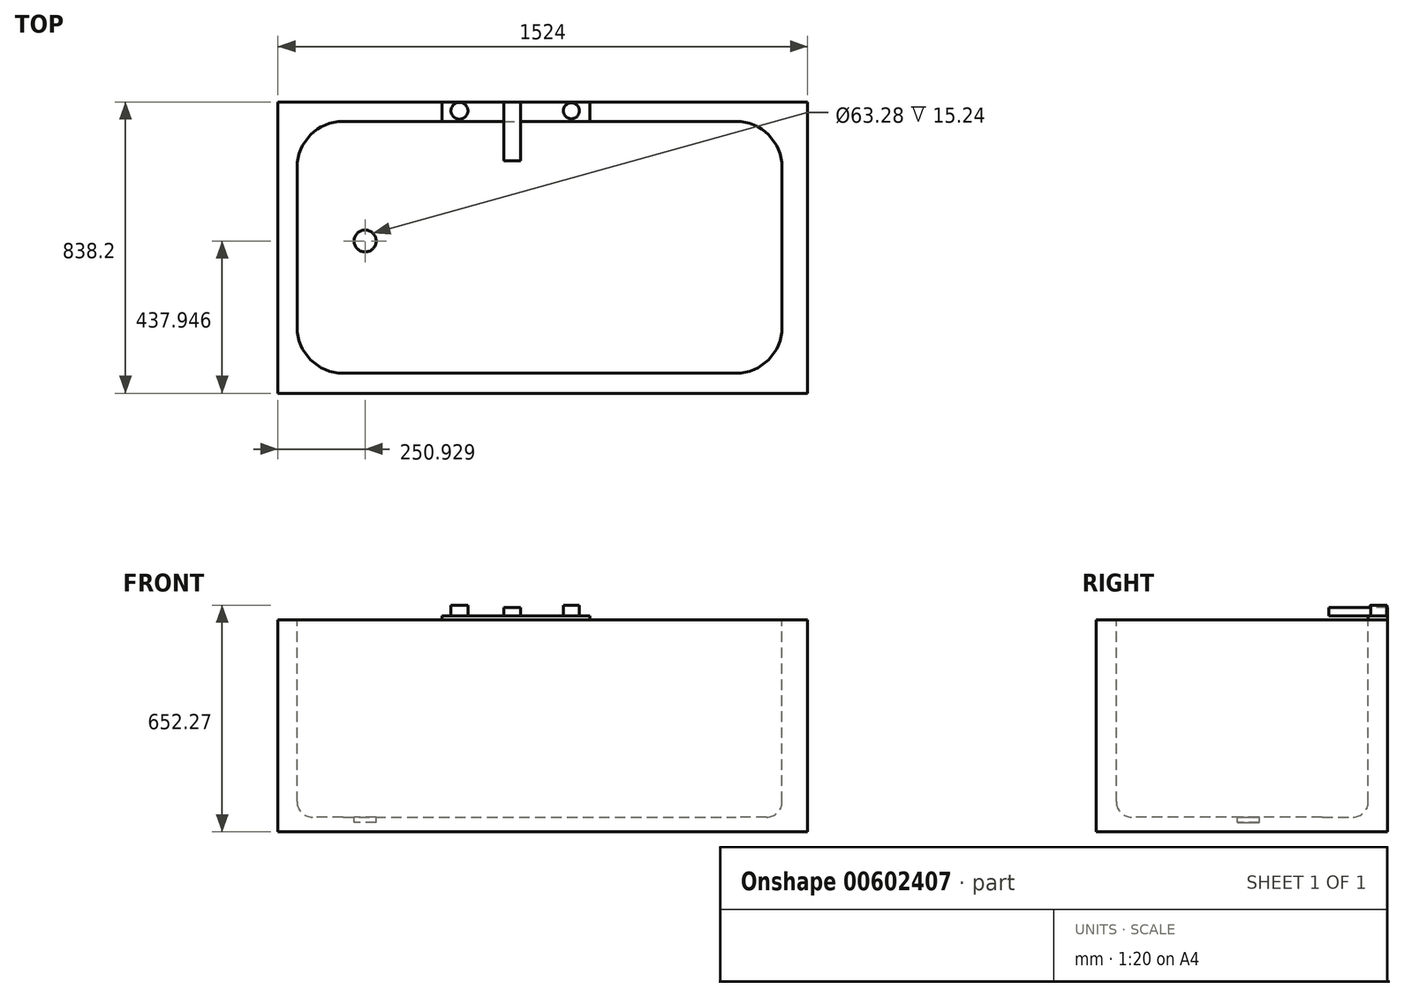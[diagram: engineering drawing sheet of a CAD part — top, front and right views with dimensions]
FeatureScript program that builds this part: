
annotation { "Feature Type Name" : "Feature", "Feature Type Description" : "" }
export const myFeature = defineFeature(function(context is Context, id is Id, definition is map)
    precondition{}
    {
        {
            var Q0;
            Q0=qCreatedBy(makeId("Top.planeOp"),FACE);
            var sketch = newSketch(context, id + "F0", { "sketchPlane" : qUnion([Q0])});
            skLineSegment(sketch, "E0.bottom", {"start": v(0, 0) * mm, "end": v(1524, 0) * mm});
            skLineSegment(sketch, "E0.top", {"start": v(0, -838.2) * mm, "end": v(1524, -838.2) * mm});
            skLineSegment(sketch, "E0.left", {"start": v(0, 0) * mm, "end": v(0, -838.2) * mm});
            skLineSegment(sketch, "E0.right", {"start": v(1524, 0) * mm, "end": v(1524, -838.2) * mm});
            skSolve(sketch);
        }
        {
            var Q0;
            Q0=makeQuery(id+"F0.imprint","IMPRINT",FACE,{"disambiguationData":[TD([[makeQuery(id+"F0.imprint","IMPRINT",EDGE,{"derivedFrom":sQuery(id+"F0.wireOp",EDGE,"E0.bottom")}),-1.0]])]});
            extrude(context, id + "F1", {"entities" : qUnion([Q0]), "depth" : 609.6 * mm, "offsetDistance" : 30.48 * mm});
        }
        {
            var Q0;
            Q0=makeQuery(id+"F1.opExtrude","CAP_FACE",FACE,{"disambiguationData":[OSD([sQuery(id+"F0.wireOp",EDGE,"E0.bottom"),sQuery(id+"F0.wireOp",EDGE,"E0.top"),sQuery(id+"F0.wireOp",EDGE,"E0.left"),sQuery(id+"F0.wireOp",EDGE,"E0.right")])],"isStart":false});
            var sketch = newSketch(context, id + "F2", { "sketchPlane" : qUnion([Q0])});
            skLineSegment(sketch, "E1.bottom", {"start": v(55.36, -55.93) * mm, "end": v(1450.41, -55.93) * mm});
            skLineSegment(sketch, "E1.top", {"start": v(55.36, -780.67) * mm, "end": v(1450.41, -780.67) * mm});
            skLineSegment(sketch, "E1.left", {"start": v(55.36, -55.93) * mm, "end": v(55.36, -780.67) * mm});
            skLineSegment(sketch, "E1.right", {"start": v(1450.41, -55.93) * mm, "end": v(1450.41, -780.67) * mm});
            skSolve(sketch);
        }
        {
            var Q0;
            Q0=makeQuery(id+"F2.imprint","IMPRINT",FACE,{"disambiguationData":[TD([[makeQuery(id+"F2.imprint","IMPRINT",EDGE,{"derivedFrom":sQuery(id+"F2.wireOp",EDGE,"E1.bottom")}),-1.0]])]});
            extrude(context, id + "F3", {"entities" : qUnion([Q0]), "operationType" : NewBodyOperationType.REMOVE, "oppositeDirection" : true, "depth" : 566.93 * mm, "offsetDistance" : 30.48 * mm});
        }
        {
            var Q0;
            Q0=makeQuery(id+"F3.boolean.opBoolean","COPY",EDGE,{"derivedFrom":makeQuery(id+"F3.opExtrude","SWEPT_EDGE",EDGE,{"disambiguationData":[OSD([sQuery(id+"F2.wireOp",EDGE,"E1.bottom"),sQuery(id+"F2.wireOp",EDGE,"E1.left")])]})});
            var Q1;
            Q1=makeQuery(id+"F3.boolean.opBoolean","COPY",EDGE,{"derivedFrom":makeQuery(id+"F3.opExtrude","SWEPT_EDGE",EDGE,{"disambiguationData":[OSD([sQuery(id+"F2.wireOp",EDGE,"E1.bottom"),sQuery(id+"F2.wireOp",EDGE,"E1.right")])]})});
            var Q2;
            Q2=makeQuery(id+"F3.boolean.opBoolean","COPY",EDGE,{"derivedFrom":makeQuery(id+"F3.opExtrude","SWEPT_EDGE",EDGE,{"disambiguationData":[OSD([sQuery(id+"F2.wireOp",EDGE,"E1.top"),sQuery(id+"F2.wireOp",EDGE,"E1.right")])]})});
            var Q3;
            Q3=makeQuery(id+"F3.boolean.opBoolean","COPY",EDGE,{"derivedFrom":makeQuery(id+"F3.opExtrude","SWEPT_EDGE",EDGE,{"disambiguationData":[OSD([sQuery(id+"F2.wireOp",EDGE,"E1.top"),sQuery(id+"F2.wireOp",EDGE,"E1.left")])]})});
            fillet(context, id + "F4", {"entities" : qUnion([Q0, Q1, Q2, Q3]), "radius" : 132.45 * mm, "tangentPropagation" : true, "allowEdgeOverflow" : false});
        }
        {
            var Q0;
            Q0=makeQuery(id+"F3.boolean.opBoolean","COPY",FACE,{"derivedFrom":makeQuery(id+"F3.opExtrude","CAP_FACE",FACE,{"disambiguationData":[OSD([sQuery(id+"F2.wireOp",EDGE,"E1.bottom"),sQuery(id+"F2.wireOp",EDGE,"E1.top"),sQuery(id+"F2.wireOp",EDGE,"E1.left"),sQuery(id+"F2.wireOp",EDGE,"E1.right")])],"isStart":false})});
            fillet(context, id + "F5", {"entities" : qUnion([Q0]), "radius" : 44.15 * mm, "tangentPropagation" : true, "allowEdgeOverflow" : false});
        }
        {
            var Q0;
            Q0=makeQuery(id+"F1.opExtrude","CAP_FACE",FACE,{"disambiguationData":[OSD([sQuery(id+"F0.wireOp",EDGE,"E0.bottom"),sQuery(id+"F0.wireOp",EDGE,"E0.top"),sQuery(id+"F0.wireOp",EDGE,"E0.left"),sQuery(id+"F0.wireOp",EDGE,"E0.right")])],"isStart":false});
            var sketch = newSketch(context, id + "F6", { "sketchPlane" : qUnion([Q0])});
            skLineSegment(sketch, "E2.bottom", {"start": v(471.72, 0) * mm, "end": v(897.09, 0) * mm});
            skLineSegment(sketch, "E2.top", {"start": v(471.72, -55.93) * mm, "end": v(897.09, -55.93) * mm});
            skLineSegment(sketch, "E2.left", {"start": v(471.72, 0) * mm, "end": v(471.72, -55.93) * mm});
            skLineSegment(sketch, "E2.right", {"start": v(897.09, 0) * mm, "end": v(897.09, -55.93) * mm});
            skSolve(sketch);
        }
        {
            var Q0;
            Q0=makeQuery(id+"F6.imprint","IMPRINT",FACE,{"disambiguationData":[TD([[makeQuery(id+"F6.imprint","IMPRINT",EDGE,{"derivedFrom":sQuery(id+"F6.wireOp",EDGE,"E2.bottom")}),-1.0]])]});
            extrude(context, id + "F7", {"entities" : qUnion([Q0]), "operationType" : NewBodyOperationType.ADD, "depth" : 12.2 * mm, "offsetDistance" : 30.48 * mm});
        }
        {
            var Q0;
            Q0=makeQuery(id+"F7.opExtrude","CAP_FACE",FACE,{"disambiguationData":[OSD([sQuery(id+"F6.wireOp",EDGE,"E2.bottom"),sQuery(id+"F6.wireOp",EDGE,"E2.top"),sQuery(id+"F6.wireOp",EDGE,"E2.left"),sQuery(id+"F6.wireOp",EDGE,"E2.right")])],"isStart":false});
            var sketch = newSketch(context, id + "F8", { "sketchPlane" : qUnion([Q0])});
            skCircle(sketch, "E3", {"center": v(522.36, -25.52) * mm, "radius": 24.3 * mm});
            skCircle(sketch, "E4", {"center": v(844.42, -25.52) * mm, "radius": 23.1 * mm});
            skSolve(sketch);
        }
        {
            var Q0;
            Q0=makeQuery(id+"F8.imprint","IMPRINT",FACE,{"disambiguationData":[TD([[makeQuery(id+"F8.imprint","IMPRINT",EDGE,{"derivedFrom":sQuery(id+"F8.wireOp",EDGE,"E3")}),1.0]])]});
            var Q1;
            Q1=makeQuery(id+"F8.imprint","IMPRINT",FACE,{"disambiguationData":[TD([[makeQuery(id+"F8.imprint","IMPRINT",EDGE,{"derivedFrom":sQuery(id+"F8.wireOp",EDGE,"E4")}),1.0]])]});
            extrude(context, id + "F9", {"entities" : qUnion([Q0, Q1]), "operationType" : NewBodyOperationType.ADD, "depth" : 30.48 * mm, "offsetDistance" : 30.48 * mm});
        }
        {
            var Q0;
            Q0=makeQuery(id+"F7.opExtrude","CAP_FACE",FACE,{"disambiguationData":[OSD([sQuery(id+"F6.wireOp",EDGE,"E2.bottom"),sQuery(id+"F6.wireOp",EDGE,"E2.top"),sQuery(id+"F6.wireOp",EDGE,"E2.left"),sQuery(id+"F6.wireOp",EDGE,"E2.right")])],"isStart":false});
            var sketch = newSketch(context, id + "F10", { "sketchPlane" : qUnion([Q0])});
            skLineSegment(sketch, "E5.bottom", {"start": v(649.97, 0) * mm, "end": v(698.58, 0) * mm});
            skLineSegment(sketch, "E5.top", {"start": v(649.97, -169.34) * mm, "end": v(698.58, -169.34) * mm});
            skLineSegment(sketch, "E5.left", {"start": v(649.97, 0) * mm, "end": v(649.97, -169.34) * mm});
            skLineSegment(sketch, "E5.right", {"start": v(698.58, 0) * mm, "end": v(698.58, -169.34) * mm});
            skSolve(sketch);
        }
        {
            var Q0;
            Q0 = qSketchRegion(id + "F10", true);
            extrude(context, id + "F11", {"entities" : qUnion([Q0]), "operationType" : NewBodyOperationType.ADD, "depth" : 24.38 * mm, "offsetDistance" : 30.48 * mm});
        }
        {
            var Q0;
            Q0=makeQuery(id+"F3.boolean.opBoolean","COPY",FACE,{"derivedFrom":makeQuery(id+"F3.opExtrude","CAP_FACE",FACE,{"disambiguationData":[OSD([sQuery(id+"F2.wireOp",EDGE,"E1.bottom"),sQuery(id+"F2.wireOp",EDGE,"E1.top"),sQuery(id+"F2.wireOp",EDGE,"E1.left"),sQuery(id+"F2.wireOp",EDGE,"E1.right")])],"isStart":false})});
            var sketch = newSketch(context, id + "F12", { "sketchPlane" : qUnion([Q0])});
            skCircle(sketch, "E6", {"center": v(250.93, -400.25) * mm, "radius": 31.64 * mm});
            skSolve(sketch);
        }
        {
            var Q0;
            Q0=makeQuery(id+"F12.imprint","IMPRINT",FACE,{"disambiguationData":[TD([[makeQuery(id+"F12.imprint","IMPRINT",EDGE,{"derivedFrom":sQuery(id+"F12.wireOp",EDGE,"E6")}),1.0]])]});
            extrude(context, id + "F13", {"entities" : qUnion([Q0]), "operationType" : NewBodyOperationType.REMOVE, "oppositeDirection" : true, "depth" : 15.24 * mm, "offsetDistance" : 30.48 * mm});
        }
    });
